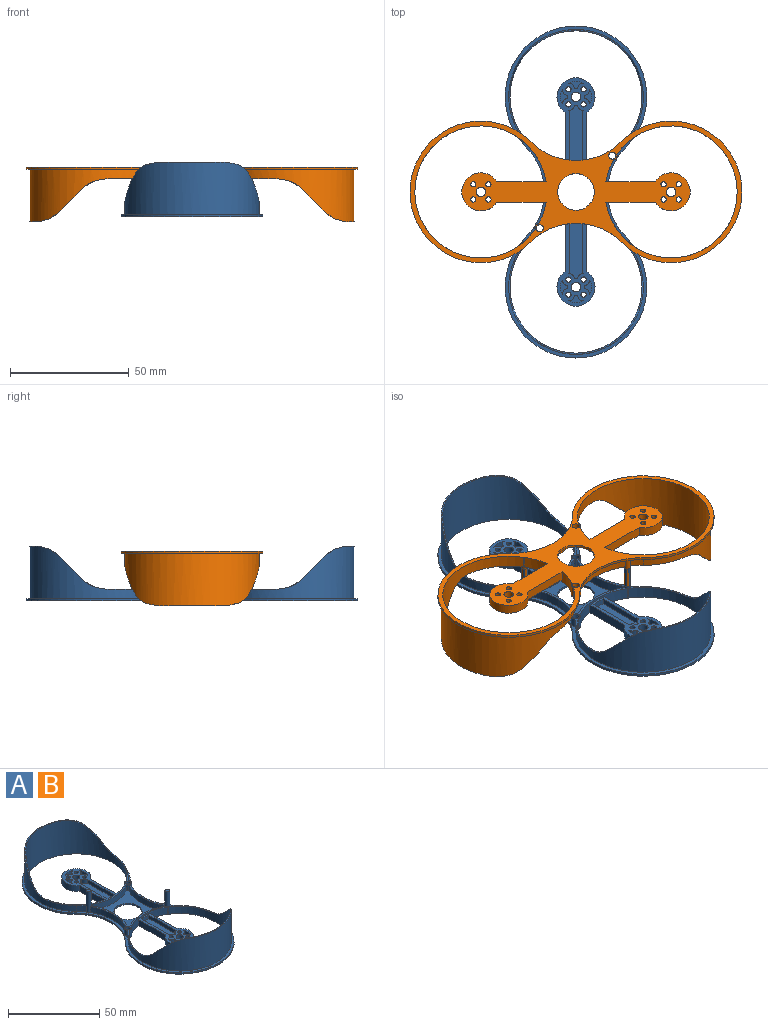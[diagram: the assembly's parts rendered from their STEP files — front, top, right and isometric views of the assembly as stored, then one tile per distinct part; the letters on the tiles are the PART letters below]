
ASSEMBLY  parts=2 mates=1
PART A: 120 faces, bbox 59.6x139.6x23 mm
  f0: plane 139.57x59.57mm, normal (0,0,-1), area 1906.9mm2, adj f1,f5,f16,f17,f18,f26,f29,f31
  f1: cylinder r=27.75mm len=27.61mm, axis (0,0,-1), area 110.2mm2, adj f0,f10,f26,f29,f32,f33,f34
  f2: cylinder r=28.28mm len=4mm, axis (0,0,-1), area 19.1mm2, adj f9,f10,f15,f30
  f3: cylinder r=28.28mm len=27.17mm, axis (0,0,-1), area 113.4mm2, adj f9,f10,f30,f80
  f4: cylinder r=29.28mm len=27.84mm, axis (0,0,-1), area 116mm2, adj f10,f19,f28,f80
  f5: cylinder r=27.75mm len=55.5mm, axis (0,0,-1), area 1857.3mm2, adj f0,f10,f13,f14,f20,f21,f22,f23
  f6: cylinder r=28.75mm len=27.33mm, axis (0,0,-1), area 113.9mm2, adj f10,f19,f26,f28
  f7: cylinder r=28.28mm len=27.17mm, axis (0,0,-1), area 113.4mm2, adj f9,f11,f26,f84
  f8: cylinder r=29.28mm len=27.84mm, axis (0,0,-1), area 116mm2, adj f11,f19,f26,f82
  f9: plane 139.57x59.57mm, normal (0,0,1), area 532.2mm2, adj f2,f3,f7,f12,f15,f16,f17,f18
  f10: plane 49.99x42.29mm, normal (0,0,1), area 75.9mm2, adj f1,f2,f3,f4,f5,f6,f15,f22
  f11: plane 49.99x42.29mm, normal (0,0,1), area 75.9mm2, adj f7,f8,f26,f65,f66,f67,f68,f72
  f12: cylinder r=28.28mm len=4.25mm, axis (0,0,-1), area 22.1mm2, adj f9,f13,f15,f26
  f13: plane 20.04x13.18mm, normal (0,0,1), area 14.4mm2, adj f5,f12,f15,f23,f26
  f14: plane 21.25x2.07mm, normal (0,0,1), area 10.8mm2, adj f5,f15,f24,f25
  f15: cylinder r=28.28mm len=56.57mm, axis (0,0,-1), area 1712.1mm2, adj f2,f9,f10,f12,f13,f14,f20,f21
  f16: cylinder r=26.78mm len=37.88mm, axis (0,0,-1), area 42.1mm2, adj f0,f9,f17,f73
  f17: cylinder r=29.78mm len=59.57mm, axis (0,0,-1), area 140.4mm2, adj f0,f9,f16,f18
  f18: cylinder r=26.78mm len=37.88mm, axis (0,0,-1), area 42.1mm2, adj f0,f9,f17,f73
  f19: plane 29.73x28.79mm, normal (0,0,1), area 389.8mm2, adj f4,f6,f8,f26,f28,f68,f80,f82
  f20: plane 9.21x9.21mm, normal (0,0.71,0.71), area 7.6mm2, adj f5,f15,f23,f24
  f21: plane 9.21x9.21mm, normal (0,0.71,0.71), area 7.6mm2, adj f5,f15,f22,f25
  f22: cylinder r=15mm len=10.61mm, axis (1,0,0), area 6.3mm2, adj f5,f10,f15,f21
  f23: cylinder r=15mm len=10.61mm, axis (1,0,0), area 6.3mm2, adj f5,f13,f15,f20
  f24: cylinder r=15mm len=14.48mm, axis (-1,0,0), area 10.1mm2, adj f5,f14,f15,f20
  f25: cylinder r=15mm len=14.48mm, axis (-1,0,0), area 10.1mm2, adj f5,f14,f15,f21
  f26: cylinder r=1.35mm len=15mm, axis (0,0,-1), area 100.8mm2, adj f0,f1,f5,f6,f7,f8,f9,f10
  f27: plane 2.7x2.7mm, normal (0,0,1), area 5.7mm2, adj f26
  f28: cylinder r=2mm len=4mm, axis (0,0,-1), area 4.7mm2, adj f4,f6,f10,f19
  f29: cylinder r=2mm len=5mm, axis (0,0,-1), area 16.5mm2, adj f0,f1,f5,f10
  f30: cylinder r=2mm len=4mm, axis (0,0,-1), area 18.2mm2, adj f2,f3,f9,f10
  f31: cylinder r=1.5mm len=5mm, axis (0,0,-1), area 47.1mm2, adj f0,f10
  f32: plane 35.75x16mm, normal (0,0,1), area 197.4mm2, adj f1,f33,f34,f35,f36,f37,f38,f39
  f33: plane 20.66x4mm, normal (1,0,0), area 82.6mm2, adj f0,f1,f32,f39
  f34: plane 20.66x4mm, normal (-1,0,0), area 82.6mm2, adj f0,f1,f32,f39
  f35: cylinder r=1.1mm len=4mm, axis (0,0,-1), area 27.6mm2, adj f0,f32
  f36: cylinder r=1.1mm len=4mm, axis (0,0,-1), area 27.6mm2, adj f0,f32
  f37: cylinder r=1.1mm len=4mm, axis (0,0,-1), area 27.6mm2, adj f0,f32
  f38: cylinder r=1.1mm len=4mm, axis (0,0,-1), area 27.6mm2, adj f0,f32
  f39: cylinder r=8mm len=16mm, axis (0,0,-1), area 164.9mm2, adj f0,f32,f33,f34
  f40: cylinder r=2mm len=4mm, axis (0,0,-1), area 50.3mm2, adj f0,f32
  f41: cylinder r=2.6mm len=2.5mm, axis (0,0,-1), area 9mm2, adj f32,f42,f43,f44
  f42: plane 5.97x3.05mm, normal (0,0,1), area 8.4mm2, adj f41,f43,f44,f45
  f43: cylinder r=6.5mm len=5.97mm, axis (0,0,-1), area 15.5mm2, adj f32,f41,f42,f45
  f44: cylinder r=3.5mm len=2.5mm, axis (0,0,-1), area 3mm2, adj f32,f41,f42,f45
  f45: cylinder r=2.6mm len=2.5mm, axis (0,0,-1), area 9mm2, adj f32,f42,f43,f44
  f46: plane 5.97x3.05mm, normal (0,0,1), area 8.4mm2, adj f47,f48,f49,f50
  f47: cylinder r=3.5mm len=2.5mm, axis (0,0,-1), area 3mm2, adj f32,f46,f48,f50
  f48: cylinder r=2.6mm len=2.5mm, axis (0,0,-1), area 9mm2, adj f32,f46,f47,f49
  f49: cylinder r=6.5mm len=5.97mm, axis (0,0,-1), area 15.5mm2, adj f32,f46,f48,f50
  f50: cylinder r=2.6mm len=2.5mm, axis (0,0,-1), area 9mm2, adj f32,f46,f47,f49
  f51: cylinder r=3.5mm len=2.5mm, axis (0,0,-1), area 3mm2, adj f32,f53,f57,f58
  f52: cylinder r=6.5mm len=2.5mm, axis (0,0,-1), area 0.6mm2, adj f32,f53,f56,f57
  f53: plane 23.34x5.97mm, normal (0,0,1), area 122.2mm2, adj f51,f52,f54,f55,f56,f57,f58,f59
  f54: plane 20.77x2.5mm, normal (-1,0,0), area 51.9mm2, adj f32,f53,f55,f59
  f55: cylinder r=26.78mm len=5.56mm, axis (0,0,-1), area 13.9mm2, adj f32,f53,f54,f56
  f56: plane 20.77x2.5mm, normal (1,0,0), area 51.9mm2, adj f32,f52,f53,f55
  f57: cylinder r=2.6mm len=2.5mm, axis (0,0,-1), area 9mm2, adj f32,f51,f52,f53
  f58: cylinder r=2.6mm len=2.5mm, axis (0,0,-1), area 9mm2, adj f32,f51,f53,f59
  f59: cylinder r=6.5mm len=2.5mm, axis (0,0,-1), area 0.6mm2, adj f32,f53,f54,f58
  f60: plane 5.97x3.05mm, normal (0,0,1), area 8.4mm2, adj f61,f62,f63,f64
  f61: cylinder r=3.5mm len=2.5mm, axis (0,0,-1), area 3mm2, adj f32,f60,f62,f63
  f62: cylinder r=2.6mm len=2.5mm, axis (0,0,-1), area 9mm2, adj f32,f60,f61,f64
  f63: cylinder r=2.6mm len=2.5mm, axis (0,0,-1), area 9mm2, adj f32,f60,f61,f64
  f64: cylinder r=6.5mm len=5.97mm, axis (0,0,-1), area 15.5mm2, adj f32,f60,f62,f63
  f65: cylinder r=27.75mm len=27.61mm, axis (0,0,-1), area 110.2mm2, adj f0,f11,f80,f83,f86,f87,f88
  f66: cylinder r=28.28mm len=4mm, axis (0,0,-1), area 19.1mm2, adj f9,f11,f72,f84
  f67: cylinder r=27.75mm len=55.5mm, axis (0,0,-1), area 1857.3mm2, adj f0,f11,f70,f71,f74,f75,f76,f77
  f68: cylinder r=28.75mm len=27.33mm, axis (0,0,-1), area 113.9mm2, adj f11,f19,f80,f82
  f69: cylinder r=28.28mm len=4.25mm, axis (0,0,-1), area 22.1mm2, adj f9,f70,f72,f80
  f70: plane 20.04x13.18mm, normal (0,0,1), area 14.4mm2, adj f67,f69,f72,f77,f80
  f71: plane 21.25x2.07mm, normal (0,0,1), area 10.8mm2, adj f67,f72,f78,f79
  f72: cylinder r=28.28mm len=56.57mm, axis (0,0,-1), area 1712.1mm2, adj f9,f11,f66,f69,f70,f71,f74,f75
  f73: cylinder r=29.78mm len=59.57mm, axis (0,0,-1), area 140.4mm2, adj f0,f9,f16,f18
  f74: plane 9.21x9.21mm, normal (0,-0.71,0.71), area 7.6mm2, adj f67,f72,f77,f78
  f75: plane 9.21x9.21mm, normal (0,-0.71,0.71), area 7.6mm2, adj f67,f72,f76,f79
  f76: cylinder r=15mm len=10.61mm, axis (-1,0,0), area 6.3mm2, adj f11,f67,f72,f75
  f77: cylinder r=15mm len=10.61mm, axis (-1,0,0), area 6.3mm2, adj f67,f70,f72,f74
  f78: cylinder r=15mm len=14.48mm, axis (1,0,0), area 10.1mm2, adj f67,f71,f72,f74
  f79: cylinder r=15mm len=14.48mm, axis (1,0,0), area 10.1mm2, adj f67,f71,f72,f75
  f80: cylinder r=1.35mm len=15mm, axis (0,0,-1), area 100.8mm2, adj f0,f3,f4,f9,f10,f11,f19,f65
  f81: plane 2.7x2.7mm, normal (0,0,1), area 5.7mm2, adj f80
  f82: cylinder r=2mm len=4mm, axis (0,0,-1), area 4.7mm2, adj f8,f11,f19,f68
  f83: cylinder r=2mm len=5mm, axis (0,0,-1), area 16.5mm2, adj f0,f11,f65,f67
  f84: cylinder r=2mm len=4mm, axis (0,0,-1), area 18.2mm2, adj f7,f9,f11,f66
  f85: cylinder r=1.5mm len=5mm, axis (0,0,-1), area 47.1mm2, adj f0,f11
  f86: plane 35.75x16mm, normal (0,0,1), area 197.4mm2, adj f65,f87,f88,f89,f90,f91,f92,f93
  f87: plane 20.66x4mm, normal (-1,0,0), area 82.6mm2, adj f0,f65,f86,f93
  f88: plane 20.66x4mm, normal (1,0,0), area 82.6mm2, adj f0,f65,f86,f93
  f89: cylinder r=1.1mm len=4mm, axis (0,0,-1), area 27.6mm2, adj f0,f86
  f90: cylinder r=1.1mm len=4mm, axis (0,0,-1), area 27.6mm2, adj f0,f86
  f91: cylinder r=1.1mm len=4mm, axis (0,0,-1), area 27.6mm2, adj f0,f86
  f92: cylinder r=1.1mm len=4mm, axis (0,0,-1), area 27.6mm2, adj f0,f86
  f93: cylinder r=8mm len=16mm, axis (0,0,-1), area 164.9mm2, adj f0,f86,f87,f88
  f94: cylinder r=2mm len=4mm, axis (0,0,-1), area 50.3mm2, adj f0,f86
  f95: cylinder r=2.6mm len=2.5mm, axis (0,0,-1), area 9mm2, adj f86,f96,f97,f98
  f96: plane 5.97x3.05mm, normal (0,0,1), area 8.4mm2, adj f95,f97,f98,f99
  f97: cylinder r=6.5mm len=5.97mm, axis (0,0,-1), area 15.5mm2, adj f86,f95,f96,f99
  f98: cylinder r=3.5mm len=2.5mm, axis (0,0,-1), area 3mm2, adj f86,f95,f96,f99
  f99: cylinder r=2.6mm len=2.5mm, axis (0,0,-1), area 9mm2, adj f86,f96,f97,f98
  f100: plane 5.97x3.05mm, normal (0,0,1), area 8.4mm2, adj f101,f102,f103,f104
  f101: cylinder r=3.5mm len=2.5mm, axis (0,0,-1), area 3mm2, adj f86,f100,f102,f104
  f102: cylinder r=2.6mm len=2.5mm, axis (0,0,-1), area 9mm2, adj f86,f100,f101,f103
  f103: cylinder r=6.5mm len=5.97mm, axis (0,0,-1), area 15.5mm2, adj f86,f100,f102,f104
  f104: cylinder r=2.6mm len=2.5mm, axis (0,0,-1), area 9mm2, adj f86,f100,f101,f103
  f105: cylinder r=3.5mm len=2.5mm, axis (0,0,-1), area 3mm2, adj f86,f107,f111,f112
  f106: cylinder r=6.5mm len=2.5mm, axis (0,0,-1), area 0.6mm2, adj f86,f107,f110,f111
  f107: plane 23.34x5.97mm, normal (0,0,1), area 122.2mm2, adj f105,f106,f108,f109,f110,f111,f112,f113
  f108: plane 20.77x2.5mm, normal (1,0,0), area 51.9mm2, adj f86,f107,f109,f113
  f109: cylinder r=26.78mm len=5.56mm, axis (0,0,-1), area 13.9mm2, adj f86,f107,f108,f110
  f110: plane 20.77x2.5mm, normal (-1,0,0), area 51.9mm2, adj f86,f106,f107,f109
  f111: cylinder r=2.6mm len=2.5mm, axis (0,0,-1), area 9mm2, adj f86,f105,f106,f107
  f112: cylinder r=2.6mm len=2.5mm, axis (0,0,-1), area 9mm2, adj f86,f105,f107,f113
  f113: cylinder r=6.5mm len=2.5mm, axis (0,0,-1), area 0.6mm2, adj f86,f107,f108,f112
  f114: plane 5.97x3.05mm, normal (0,0,1), area 8.4mm2, adj f115,f116,f117,f118
  f115: cylinder r=3.5mm len=2.5mm, axis (0,0,-1), area 3mm2, adj f86,f114,f116,f117
  f116: cylinder r=2.6mm len=2.5mm, axis (0,0,-1), area 9mm2, adj f86,f114,f115,f118
  f117: cylinder r=2.6mm len=2.5mm, axis (0,0,-1), area 9mm2, adj f86,f114,f115,f118
  f118: cylinder r=6.5mm len=5.97mm, axis (0,0,-1), area 15.5mm2, adj f86,f114,f116,f117
  f119: cylinder r=7.71mm len=15.41mm, axis (0,0,-1), area 48.4mm2, adj f0,f19
PART B: same geometry as A
PLACE A at identity
PLACE B rot(axis=(0.71,-0.71,0),180deg) t=(0,0,21)mm
MATE revolute B.f119 <-> A.f119  axis (0,0,1) through (0,0,21)mm
